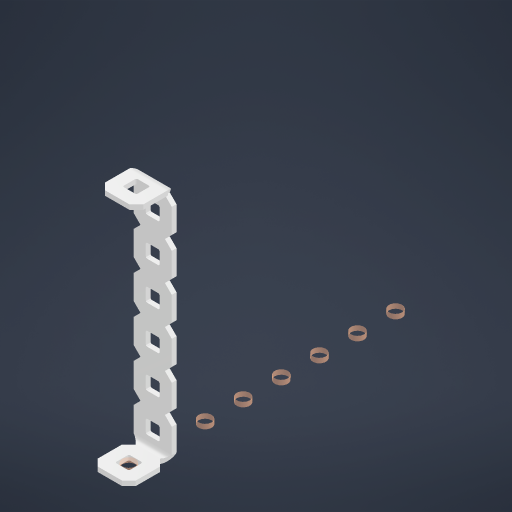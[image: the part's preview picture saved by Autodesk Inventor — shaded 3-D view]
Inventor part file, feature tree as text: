
AUTODESK INVENTOR PART (.ipt)
format: ipt  version: 2024 (Build 280153000, 153)  size: 420,352 bytes
history: native  units: in
note: dims shown in document units (in); Inventor stores cm internally (conversion verified against a paired STEP export)
features: other x11, extrude x7, sketch x2, pattern_linear x1
ambient origin geometry x8: Origin, YZ Plane, XZ Plane, XY Plane, X Axis, Y Axis, Z Axis, Center Point
bodies: Solid1 (feature_tree), Body (feature_tree)
feature tree (21):
  pattern_linear  "Rectangular Pattern1"  Spacing1=0.09in  [1 undecoded]
  other  "Bend Part1"
  other  "Bend Part2"
  other  "Srf1"
  other  "Srf126"
  other  "Srf127"
  other  "Srf128"
  other  "Srf129"
  other  "Srf130"
  other  "Srf131"
  other  "Srf250"
  sketch  "Sketch3"  dims[d1=0.5in]
  sketch  "Sketch4"  dims[d2=0.182in d3=0.09in d4=0.09in d5=0.09in d6=0.09in d7=0.09in d8=0.09in d9=0.09in d10=0.09in d11=0.02in d13=0.0in d14=0.172in d15=0.0625in d16=0.0in d19=0.5in d22=0.5in d23=0.0625in d24=90.0deg d25=0.0625in d26=90.0deg]
  other  "Circle"
  extrude  "ExtrusionSrf126"  Depth=0.0625in
  extrude  "ExtrusionSrf127"  Depth=0.0625in
  extrude  "ExtrusionSrf128"  Depth=0.0625in
  extrude  "ExtrusionSrf129"  Depth=0.0625in
  extrude  "ExtrusionSrf130"  Depth=0.0625in
  extrude  "ExtrusionSrf131"  Depth=0.0625in
  extrude  "ExtrusionSrf250"  Depth=0.0625in
note: 1 required parameter value undecoded (feature->parameter linkage not recoverable at this tier; creation-order binding heuristic only, values carry confidence <= 0.55)
